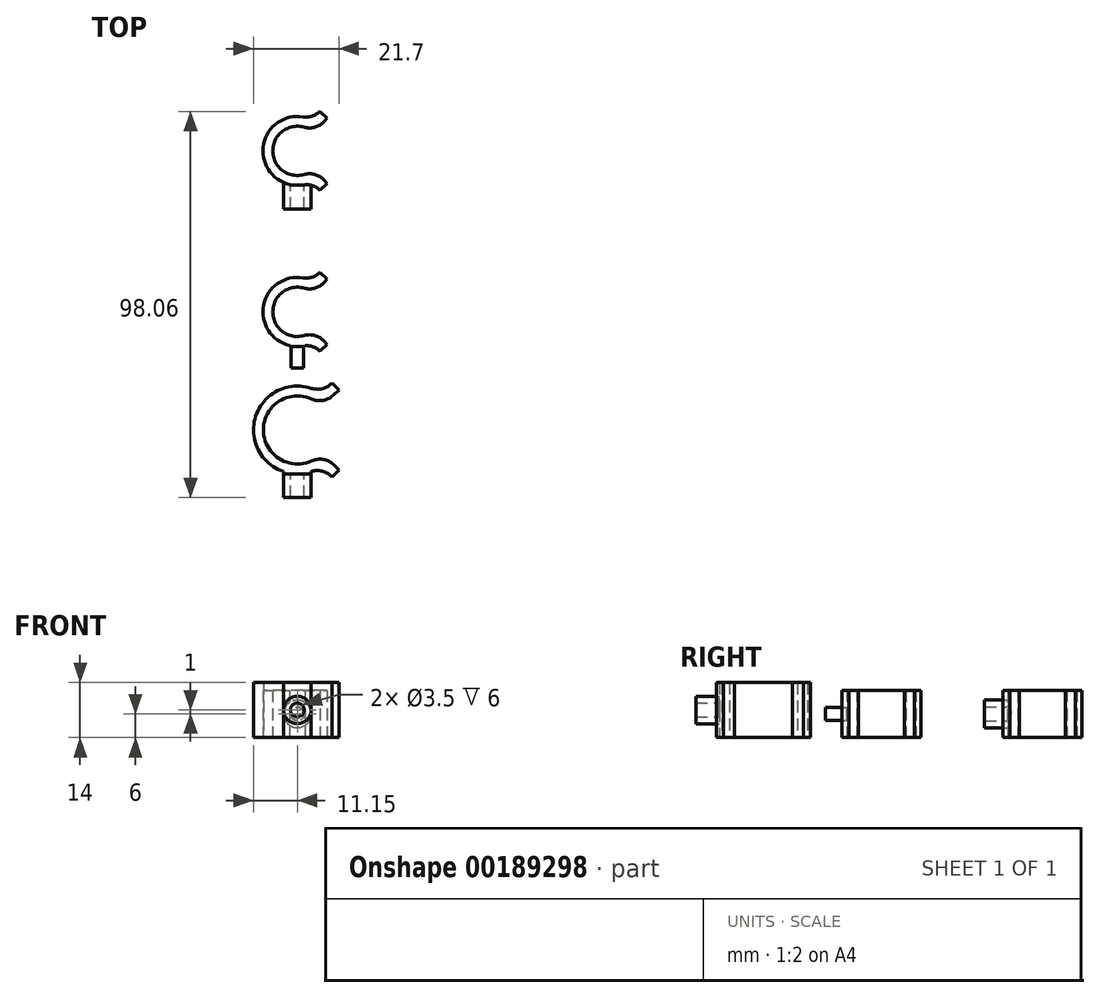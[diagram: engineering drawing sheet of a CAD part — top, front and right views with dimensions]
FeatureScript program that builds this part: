
annotation { "Feature Type Name" : "Feature", "Feature Type Description" : "" }
export const myFeature = defineFeature(function(context is Context, id is Id, definition is map)
    precondition{}
    {
        {
            var Q0;
            Q0=qCreatedBy(makeId("Top.planeOp"),FACE);
            var sketch = newSketch(context, id + "F0", { "sketchPlane" : qUnion([Q0])});
            skArc(sketch, "E0", {"start": v(4.2, 4.63) * mm, "mid": v(-6.25, 0) * mm, "end": v(4.2, -4.63) * mm});
            skPoint(sketch, "E1", {"position": v(4.2, -4.63) * mm});
            skPoint(sketch, "E2", {"position": v(4.2, 4.63) * mm});
            skArc(sketch, "E3", {"start": v(3.79, 7.89) * mm, "mid": v(-8.25, 2.91) * mm, "end": v(-2, -8.52) * mm});
            skLineSegment(sketch, "E4", {"start": v(4.2, 4.63) * mm, "end": v(-0.45, 8.86) * mm, "construction": true});
            skLineSegment(sketch, "E5", {"start": v(4.2, -4.63) * mm, "end": v(1.78, -6.83) * mm, "construction": true});
            skLineSegment(sketch, "E6", {"start": v(4.2, 4.63) * mm, "end": v(7.57, 8.33) * mm});
            skLineSegment(sketch, "E7", {"start": v(4.2, -4.63) * mm, "end": v(7.57, -8.32) * mm});
            skLineSegment(sketch, "E8", {"start": v(7.57, 8.33) * mm, "end": v(5.72, 10) * mm});
            skLineSegment(sketch, "E9", {"start": v(5.72, 10) * mm, "end": v(3.79, 7.89) * mm});
            skLineSegment(sketch, "E10", {"start": v(7.57, -8.32) * mm, "end": v(5.72, -10) * mm});
            skLineSegment(sketch, "E11", {"start": v(5.72, -10) * mm, "end": v(3.79, -7.89) * mm});
            skLineSegment(sketch, "E12", {"start": v(2, -8.75) * mm, "end": v(-2, -8.75) * mm});
            skPoint(sketch, "E13", {"position": v(0, -8.75) * mm});
            skLineSegment(sketch, "E14", {"start": v(-2, -8.75) * mm, "end": v(-2, -8.52) * mm});
            skLineSegment(sketch, "E15", {"start": v(2, -8.75) * mm, "end": v(2, -8.52) * mm});
            skArc(sketch, "E16.trimOffspring", {"start": v(2, -8.52) * mm, "mid": v(2.91, -8.25) * mm, "end": v(3.79, -7.89) * mm});
            skArc(sketch, "E17", {"start": v(6.23, -24) * mm, "mid": v(-8.65, -30) * mm, "end": v(6.23, -36) * mm});
            skPoint(sketch, "E18", {"position": v(6.23, -36) * mm});
            skPoint(sketch, "E19", {"position": v(6.23, -24) * mm});
            skArc(sketch, "E20", {"start": v(6.1, -20.66) * mm, "mid": v(-10.05, -25.16) * mm, "end": v(-3.5, -40.59) * mm});
            skLineSegment(sketch, "E21", {"start": v(6.23, -24) * mm, "end": v(1.35, -18.93) * mm, "construction": true});
            skLineSegment(sketch, "E22", {"start": v(6.23, -36) * mm, "end": v(1.35, -41.07) * mm, "construction": true});
            skLineSegment(sketch, "E23", {"start": v(6.23, -24) * mm, "end": v(10.55, -19.84) * mm});
            skLineSegment(sketch, "E24", {"start": v(10.55, -19.84) * mm, "end": v(8.82, -18.04) * mm});
            skLineSegment(sketch, "E25", {"start": v(8.82, -18.04) * mm, "end": v(6.1, -20.66) * mm});
            skLineSegment(sketch, "E26", {"start": v(6.23, -36) * mm, "end": v(10.55, -40.16) * mm});
            skLineSegment(sketch, "E27", {"start": v(10.55, -40.16) * mm, "end": v(8.82, -41.96) * mm});
            skLineSegment(sketch, "E28", {"start": v(8.82, -41.96) * mm, "end": v(6.1, -39.34) * mm});
            skLineSegment(sketch, "E29", {"start": v(-3.5, -41.15) * mm, "end": v(3.5, -41.15) * mm});
            skPoint(sketch, "E30", {"position": v(0, -41.15) * mm});
            skLineSegment(sketch, "E31", {"start": v(-3.5, -41.15) * mm, "end": v(-3.5, -40.59) * mm});
            skLineSegment(sketch, "E32", {"start": v(3.5, -41.15) * mm, "end": v(3.5, -40.59) * mm});
            skArc(sketch, "E33.trimOffspring", {"start": v(3.5, -40.59) * mm, "mid": v(4.84, -40.05) * mm, "end": v(6.1, -39.34) * mm});
            skSolve(sketch);
        }
        {
            var Q0;
            Q0=makeQuery(id+"F0.imprint","IMPRINT",FACE,{"disambiguationData":[TD([[makeQuery(id+"F0.imprint","IMPRINT",EDGE,{"derivedFrom":sQuery(id+"F0.wireOp",EDGE,"E0")}),-1.0]])]});
            extrude(context, id + "F1", {"entities" : qUnion([Q0]), "depth" : 12 * mm, "offsetDistance" : 25 * mm});
        }
        {
            var Q0;
            Q0=makeQuery(id+"F0.imprint","IMPRINT",FACE,{"disambiguationData":[TD([[makeQuery(id+"F0.imprint","IMPRINT",EDGE,{"derivedFrom":sQuery(id+"F0.wireOp",EDGE,"E17")}),-1.0]])]});
            extrude(context, id + "F2", {"entities" : qUnion([Q0]), "depth" : 14 * mm, "offsetDistance" : 25 * mm});
        }
        {
            var Q0;
            Q0=makeQuery(id+"F2.opExtrude","SWEPT_FACE",FACE,{"disambiguationData":[OSD([sQuery(id+"F0.wireOp",EDGE,"E29")])]});
            var sketch = newSketch(context, id + "F3", { "sketchPlane" : qUnion([Q0])});
            skLineSegment(sketch, "E34", {"start": v(-3.5, 7) * mm, "end": v(3.5, 7) * mm, "construction": true});
            skPoint(sketch, "E35", {"position": v(0, 7) * mm});
            skCircle(sketch, "E36", {"center": v(0, 7) * mm, "radius": 1.75 * mm});
            skCircle(sketch, "E37", {"center": v(0, 7) * mm, "radius": 3.5 * mm});
            skSolve(sketch);
        }
        {
            var Q0;
            Q0=makeQuery(id+"F3.imprint","IMPRINT",FACE,{"disambiguationData":[TD([[makeQuery(id+"F3.imprint","IMPRINT",EDGE,{"derivedFrom":sQuery(id+"F3.wireOp",EDGE,"E36")}),-1.0]])]});
            extrude(context, id + "F4", {"entities" : qUnion([Q0]), "operationType" : NewBodyOperationType.ADD, "depth" : 6 * mm, "offsetDistance" : 25 * mm});
        }
        {
            var Q0;
            Q0=makeQuery(id+"F1.opExtrude","SWEPT_FACE",FACE,{"disambiguationData":[OSD([sQuery(id+"F0.wireOp",EDGE,"E12")])]});
            var sketch = newSketch(context, id + "F5", { "sketchPlane" : qUnion([Q0])});
            skLineSegment(sketch, "E38", {"start": v(-2, 6) * mm, "end": v(2, 6) * mm, "construction": true});
            skPoint(sketch, "E39", {"position": v(0, 6) * mm});
            skCircle(sketch, "E40", {"center": v(0, 6) * mm, "radius": 1.6 * mm});
            skSolve(sketch);
        }
        {
            var Q0;
            Q0=makeQuery(id+"F5.imprint","IMPRINT",FACE,{"disambiguationData":[TD([[makeQuery(id+"F5.imprint","IMPRINT",EDGE,{"derivedFrom":sQuery(id+"F5.wireOp",EDGE,"E40")}),1.0]])]});
            extrude(context, id + "F6", {"entities" : qUnion([Q0]), "operationType" : NewBodyOperationType.ADD, "depth" : 5.5 * mm, "offsetDistance" : 25 * mm});
        }
        {
            var Q0;
            Q0=makeQuery(id+"F1.opExtrude","SWEPT_EDGE",EDGE,{"disambiguationData":[OSD([sQuery(id+"F0.wireOp",EDGE,"E0"),sQuery(id+"F0.wireOp",EDGE,"E6")])]});
            var Q1;
            Q1=makeQuery(id+"F1.opExtrude","SWEPT_EDGE",EDGE,{"disambiguationData":[OSD([sQuery(id+"F0.wireOp",EDGE,"E0"),sQuery(id+"F0.wireOp",EDGE,"E7")])]});
            var Q2;
            Q2=makeQuery(id+"F1.opExtrude","SWEPT_EDGE",EDGE,{"disambiguationData":[OSD([sQuery(id+"F0.wireOp",EDGE,"E11"),sQuery(id+"F0.wireOp",EDGE,"E16.trimOffspring")])]});
            var Q3;
            Q3=makeQuery(id+"F1.opExtrude","SWEPT_EDGE",EDGE,{"disambiguationData":[OSD([sQuery(id+"F0.wireOp",EDGE,"E3"),sQuery(id+"F0.wireOp",EDGE,"E9")])]});
            var Q4;
            Q4=makeQuery(id+"F2.opExtrude","SWEPT_EDGE",EDGE,{"disambiguationData":[OSD([sQuery(id+"F0.wireOp",EDGE,"E17"),sQuery(id+"F0.wireOp",EDGE,"E23")])]});
            var Q5;
            Q5=makeQuery(id+"F2.opExtrude","SWEPT_EDGE",EDGE,{"disambiguationData":[OSD([sQuery(id+"F0.wireOp",EDGE,"E28"),sQuery(id+"F0.wireOp",EDGE,"E33.trimOffspring")])]});
            var Q6;
            Q6=makeQuery(id+"F2.opExtrude","SWEPT_EDGE",EDGE,{"disambiguationData":[OSD([sQuery(id+"F0.wireOp",EDGE,"E17"),sQuery(id+"F0.wireOp",EDGE,"E26")])]});
            var Q7;
            Q7=makeQuery(id+"F2.opExtrude","SWEPT_EDGE",EDGE,{"disambiguationData":[OSD([sQuery(id+"F0.wireOp",EDGE,"E20"),sQuery(id+"F0.wireOp",EDGE,"E25")])]});
            fillet(context, id + "F7", {"entities" : qUnion([Q0, Q1, Q2, Q3, Q4, Q5, Q6, Q7]), "radius" : 5 * mm, "tangentPropagation" : true, "allowEdgeOverflow" : false});
        }
        {
            var Q0;
            Q0=makeQuery(id+"F1.opExtrude","SWEPT_BODY",BODY,{"disambiguationData":[OSD([sQuery(id+"F0.wireOp",EDGE,"E0"),sQuery(id+"F0.wireOp",EDGE,"E3"),sQuery(id+"F0.wireOp",EDGE,"E6"),sQuery(id+"F0.wireOp",EDGE,"E7"),sQuery(id+"F0.wireOp",EDGE,"E8"),sQuery(id+"F0.wireOp",EDGE,"E9"),sQuery(id+"F0.wireOp",EDGE,"E10"),sQuery(id+"F0.wireOp",EDGE,"E11"),sQuery(id+"F0.wireOp",EDGE,"E12"),sQuery(id+"F0.wireOp",EDGE,"E14"),sQuery(id+"F0.wireOp",EDGE,"E15"),sQuery(id+"F0.wireOp",EDGE,"E16.trimOffspring")])]});
            transform(context, id + "F8", {"entities" : qUnion([Q0]), "transformType" : TransformType.TRANSLATION_3D, "dx" : 0 * mm, "dy" : 40.9 * mm, "dz" : 0 * mm, "makeCopy" : true});
        }
        {
            var Q0;
            Q0=makeQuery(id+"F8.opPattern","COPY",FACE,{"derivedFrom":makeQuery(id+"F1.opExtrude","SWEPT_FACE",FACE,{"disambiguationData":[OSD([sQuery(id+"F0.wireOp",EDGE,"E12")])]}),"instanceName":"1"});
            var sketch = newSketch(context, id + "F9", { "sketchPlane" : qUnion([Q0])});
            skLineSegment(sketch, "E41", {"start": v(-2, 6) * mm, "end": v(2, 6) * mm, "construction": true});
            skPoint(sketch, "E42", {"position": v(0, 6) * mm});
            skCircle(sketch, "E43", {"center": v(0, 6) * mm, "radius": 1.75 * mm});
            skCircle(sketch, "E44", {"center": v(0, 6) * mm, "radius": 3.5 * mm});
            skSolve(sketch);
        }
        {
            var Q0;
            Q0=makeQuery(id+"F8.opPattern","COPY",FACE,{"derivedFrom":makeQuery(id+"F6.opExtrude","CAP_FACE",FACE,{"disambiguationData":[OSD([sQuery(id+"F5.wireOp",EDGE,"E40")])],"isStart":false}),"instanceName":"1"});
            var sketch = newSketch(context, id + "F10", { "sketchPlane" : qUnion([Q0])});
            skCircle(sketch, "E45", {"center": v(0, 6) * mm, "radius": 1.6 * mm});
            skSolve(sketch);
        }
        {
            var Q0;
            Q0=makeQuery(id+"F10.imprint","IMPRINT",FACE,{"disambiguationData":[TD([[makeQuery(id+"F10.imprint","IMPRINT",EDGE,{"derivedFrom":sQuery(id+"F10.wireOp",EDGE,"E45")}),1.0]])]});
            var Q1;
            Q1=makeQuery(id+"F8.opPattern","COPY",FACE,{"derivedFrom":makeQuery(id+"F1.opExtrude","SWEPT_FACE",FACE,{"disambiguationData":[OSD([sQuery(id+"F0.wireOp",EDGE,"E12")])]}),"instanceName":"1"});
            extrude(context, id + "F11", {"entities" : qUnion([Q0]), "operationType" : NewBodyOperationType.REMOVE, "endBound" : BoundingType.UP_TO_SURFACE, "oppositeDirection" : true, "depth" : 25 * mm, "endBoundEntityFace" : qUnion([Q1]), "offsetDistance" : 25 * mm});
        }
        {
            var Q0;
            {var subQ0=sQuery(id+"F9.wireOp",EDGE,"E44");var subQ1=makeQuery(id+"F8.opPattern","COPY",EDGE,{"derivedFrom":makeQuery(id+"F1.opExtrude","SWEPT_EDGE",EDGE,{"disambiguationData":[OSD([sQuery(id+"F0.wireOp",EDGE,"E12"),sQuery(id+"F0.wireOp",EDGE,"E14")])]}),"instanceName":"1"});var subQ2=makeQuery(id+"F9.imprint","INTERSECT",VERTEX,{"disambiguationData":[OD(0.0)],"derivedFrom":[subQ1,subQ0]});Q0=makeQuery(id+"F9.imprint","IMPRINT",FACE,{"disambiguationData":[TD([[makeQuery(id+"F9.imprint","IMPRINT",EDGE,{"disambiguationData":[TD([[subQ2,-1.0]])],"derivedFrom":subQ0}),1.0]])]});}
            var Q1;
            Q1=makeQuery(id+"F9.imprint","IMPRINT",FACE,{"disambiguationData":[TD([[makeQuery(id+"F9.imprint","IMPRINT",EDGE,{"derivedFrom":sQuery(id+"F9.wireOp",EDGE,"E43")}),-1.0]])]});
            var Q2;
            {var subQ0=sQuery(id+"F9.wireOp",EDGE,"E44");var subQ1=makeQuery(id+"F8.opPattern","COPY",EDGE,{"derivedFrom":makeQuery(id+"F1.opExtrude","SWEPT_EDGE",EDGE,{"disambiguationData":[OSD([sQuery(id+"F0.wireOp",EDGE,"E12"),sQuery(id+"F0.wireOp",EDGE,"E15")])]}),"instanceName":"1"});var subQ2=makeQuery(id+"F9.imprint","INTERSECT",VERTEX,{"disambiguationData":[OD(0.0)],"derivedFrom":[subQ1,subQ0]});Q2=makeQuery(id+"F9.imprint","IMPRINT",FACE,{"disambiguationData":[TD([[makeQuery(id+"F9.imprint","IMPRINT",EDGE,{"disambiguationData":[TD([[subQ2,1.0]])],"derivedFrom":subQ0}),1.0]])]});}
            extrude(context, id + "F12", {"entities" : qUnion([Q0, Q1, Q2]), "operationType" : NewBodyOperationType.ADD, "depth" : 6 * mm, "offsetDistance" : 25 * mm, "hasSecondDirection" : true, "secondDirectionOppositeDirection" : true, "secondDirectionDepth" : 2 * mm});
        }
    });
